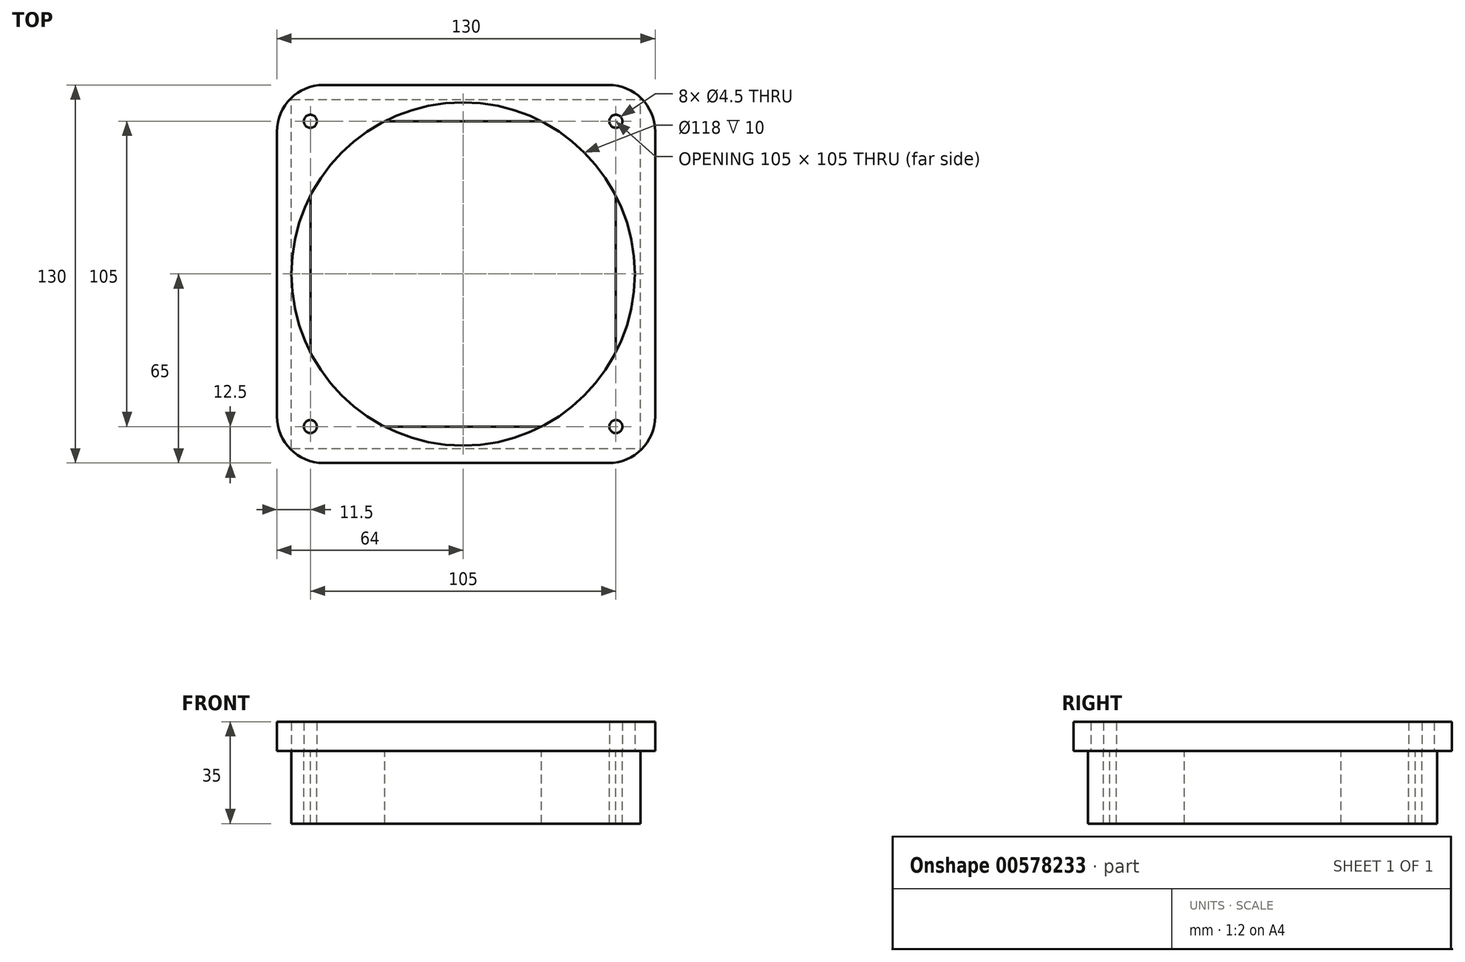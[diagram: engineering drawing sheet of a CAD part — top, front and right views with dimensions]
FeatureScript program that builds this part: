
annotation { "Feature Type Name" : "Feature", "Feature Type Description" : "" }
export const myFeature = defineFeature(function(context is Context, id is Id, definition is map)
    precondition{}
    {
        {
            var Q0;
            Q0=qCreatedBy(makeId("Top.planeOp"),FACE);
            var sketch = newSketch(context, id + "F0", { "sketchPlane" : qUnion([Q0])});
            skLineSegment(sketch, "E0.bottom", {"start": v(-59, -60) * mm, "end": v(61, -60) * mm});
            skLineSegment(sketch, "E0.top", {"start": v(-59, 60) * mm, "end": v(61, 60) * mm});
            skLineSegment(sketch, "E0.left", {"start": v(-59, -60) * mm, "end": v(-59, 60) * mm});
            skLineSegment(sketch, "E0.right", {"start": v(61, -60) * mm, "end": v(61, 60) * mm});
            skLineSegment(sketch, "E1.bottom", {"start": v(-52.5, -52.5) * mm, "end": v(52.5, -52.5) * mm});
            skLineSegment(sketch, "E1.top", {"start": v(-52.5, 52.5) * mm, "end": v(52.5, 52.5) * mm});
            skLineSegment(sketch, "E1.left", {"start": v(-52.5, -52.5) * mm, "end": v(-52.5, 52.5) * mm});
            skLineSegment(sketch, "E1.right", {"start": v(52.5, -52.5) * mm, "end": v(52.5, 52.5) * mm});
            skCircle(sketch, "E2", {"center": v(-52.5, 52.5) * mm, "radius": 2.25 * mm});
            skCircle(sketch, "E3", {"center": v(52.5, 52.5) * mm, "radius": 2.25 * mm});
            skCircle(sketch, "E4", {"center": v(-52.5, -52.5) * mm, "radius": 2.25 * mm});
            skCircle(sketch, "E5", {"center": v(52.5, -52.5) * mm, "radius": 2.25 * mm});
            skCircle(sketch, "E6", {"center": v(0, 0) * mm, "radius": 59 * mm});
            skLineSegment(sketch, "E7.0", {"start": v(-64, -65) * mm, "end": v(-64, 65) * mm});
            skLineSegment(sketch, "E7.1", {"start": v(-64, -65) * mm, "end": v(66, -65) * mm});
            skLineSegment(sketch, "E7.2", {"start": v(66, -65) * mm, "end": v(66, 65) * mm});
            skLineSegment(sketch, "E7.3", {"start": v(-64, 65) * mm, "end": v(66, 65) * mm});
            skSolve(sketch);
        }
        {
            var Q0;
            {var subQ0=sQuery(id+"F0.wireOp",EDGE,"E2");var subQ1=sQuery(id+"F0.wireOp",EDGE,"E1.top");var subQ2=makeQuery(id+"F0.imprint","INTERSECT",VERTEX,{"derivedFrom":[subQ1,subQ0]});Q0=makeQuery(id+"F0.imprint","IMPRINT",FACE,{"disambiguationData":[TD([[makeQuery(id+"F0.imprint","IMPRINT",EDGE,{"disambiguationData":[TD([[subQ2,-1.0]])],"derivedFrom":subQ1}),-1.0]])]});}
            var Q1;
            {var subQ16=sQuery(id+"F0.wireOp",EDGE,"E0.bottom");Q1=makeQuery(id+"F0.imprint","IMPRINT",FACE,{"disambiguationData":[TD([[makeQuery(id+"F0.imprint","IMPRINT",EDGE,{"derivedFrom":subQ16}),1.0]])]});}
            var Q2;
            {var subQ0=sQuery(id+"F0.wireOp",EDGE,"E4");var subQ1=sQuery(id+"F0.wireOp",EDGE,"E1.bottom");var subQ2=makeQuery(id+"F0.imprint","INTERSECT",VERTEX,{"derivedFrom":[subQ1,subQ0]});Q2=makeQuery(id+"F0.imprint","IMPRINT",FACE,{"disambiguationData":[TD([[makeQuery(id+"F0.imprint","IMPRINT",EDGE,{"disambiguationData":[TD([[subQ2,-1.0]])],"derivedFrom":subQ1}),1.0]])]});}
            var Q3;
            {var subQ0=sQuery(id+"F0.wireOp",EDGE,"E6");var subQ1=sQuery(id+"F0.wireOp",EDGE,"E1.bottom");var subQ2=makeQuery(id+"F0.imprint","INTERSECT",VERTEX,{"disambiguationData":[OD(0.0)],"derivedFrom":[subQ1,subQ0]});Q3=makeQuery(id+"F0.imprint","IMPRINT",FACE,{"disambiguationData":[TD([[makeQuery(id+"F0.imprint","IMPRINT",EDGE,{"disambiguationData":[TD([[subQ2,-1.0]])],"derivedFrom":subQ1}),-1.0]])]});}
            var Q4;
            {var subQ0=sQuery(id+"F0.wireOp",EDGE,"E6");var subQ1=sQuery(id+"F0.wireOp",EDGE,"E1.top");var subQ2=makeQuery(id+"F0.imprint","INTERSECT",VERTEX,{"disambiguationData":[OD(0.0)],"derivedFrom":[subQ1,subQ0]});Q4=makeQuery(id+"F0.imprint","IMPRINT",FACE,{"disambiguationData":[TD([[makeQuery(id+"F0.imprint","IMPRINT",EDGE,{"disambiguationData":[TD([[subQ2,-1.0]])],"derivedFrom":subQ1}),1.0]])]});}
            var Q5;
            {var subQ0=sQuery(id+"F0.wireOp",EDGE,"E6");var subQ1=sQuery(id+"F0.wireOp",EDGE,"E1.top");var subQ2=makeQuery(id+"F0.imprint","INTERSECT",VERTEX,{"disambiguationData":[OD(1.0)],"derivedFrom":[subQ1,subQ0]});Q5=makeQuery(id+"F0.imprint","IMPRINT",FACE,{"disambiguationData":[TD([[makeQuery(id+"F0.imprint","IMPRINT",EDGE,{"disambiguationData":[TD([[subQ2,-1.0]])],"derivedFrom":subQ1}),-1.0]])]});}
            var Q6;
            {var subQ0=sQuery(id+"F0.wireOp",EDGE,"E6");var subQ1=sQuery(id+"F0.wireOp",EDGE,"E1.right");var subQ2=makeQuery(id+"F0.imprint","INTERSECT",VERTEX,{"disambiguationData":[OD(0.0)],"derivedFrom":[subQ1,subQ0]});Q6=makeQuery(id+"F0.imprint","IMPRINT",FACE,{"disambiguationData":[TD([[makeQuery(id+"F0.imprint","IMPRINT",EDGE,{"disambiguationData":[TD([[subQ2,-1.0]])],"derivedFrom":subQ1}),-1.0]])]});}
            var Q7;
            {var subQ0=sQuery(id+"F0.wireOp",EDGE,"E6");var subQ1=sQuery(id+"F0.wireOp",EDGE,"E1.bottom");var subQ2=makeQuery(id+"F0.imprint","INTERSECT",VERTEX,{"disambiguationData":[OD(1.0)],"derivedFrom":[subQ1,subQ0]});Q7=makeQuery(id+"F0.imprint","IMPRINT",FACE,{"disambiguationData":[TD([[makeQuery(id+"F0.imprint","IMPRINT",EDGE,{"disambiguationData":[TD([[subQ2,-1.0]])],"derivedFrom":subQ1}),1.0]])]});}
            var Q8;
            {var subQ0=sQuery(id+"F0.wireOp",EDGE,"E6");var subQ1=sQuery(id+"F0.wireOp",EDGE,"E1.left");var subQ2=makeQuery(id+"F0.imprint","INTERSECT",VERTEX,{"disambiguationData":[OD(0.0)],"derivedFrom":[subQ1,subQ0]});Q8=makeQuery(id+"F0.imprint","IMPRINT",FACE,{"disambiguationData":[TD([[makeQuery(id+"F0.imprint","IMPRINT",EDGE,{"disambiguationData":[TD([[subQ2,-1.0]])],"derivedFrom":subQ1}),1.0]])]});}
            extrude(context, id + "F1", {"entities" : qUnion([Q0, Q1, Q2, Q3, Q4, Q5, Q6, Q7, Q8]), "oppositeDirection" : true, "depth" : 25 * mm, "offsetDistance" : 25 * mm});
        }
        {
            var Q0;
            {var subQ3=sQuery(id+"F0.wireOp",EDGE,"E0.bottom");Q0=makeQuery(id+"F0.imprint","IMPRINT",FACE,{"disambiguationData":[TD([[makeQuery(id+"F0.imprint","IMPRINT",EDGE,{"derivedFrom":subQ3}),-1.0]])]});}
            var Q1;
            {var subQ0=sQuery(id+"F0.wireOp",EDGE,"E2");var subQ1=sQuery(id+"F0.wireOp",EDGE,"E1.top");var subQ2=makeQuery(id+"F0.imprint","INTERSECT",VERTEX,{"derivedFrom":[subQ1,subQ0]});Q1=makeQuery(id+"F0.imprint","IMPRINT",FACE,{"disambiguationData":[TD([[makeQuery(id+"F0.imprint","IMPRINT",EDGE,{"disambiguationData":[TD([[subQ2,-1.0]])],"derivedFrom":subQ1}),-1.0]])]});}
            var Q2;
            {var subQ16=sQuery(id+"F0.wireOp",EDGE,"E0.bottom");Q2=makeQuery(id+"F0.imprint","IMPRINT",FACE,{"disambiguationData":[TD([[makeQuery(id+"F0.imprint","IMPRINT",EDGE,{"derivedFrom":subQ16}),1.0]])]});}
            var Q3;
            {var subQ0=sQuery(id+"F0.wireOp",EDGE,"E6");var subQ1=sQuery(id+"F0.wireOp",EDGE,"E1.top");var subQ2=makeQuery(id+"F0.imprint","INTERSECT",VERTEX,{"disambiguationData":[OD(1.0)],"derivedFrom":[subQ1,subQ0]});Q3=makeQuery(id+"F0.imprint","IMPRINT",FACE,{"disambiguationData":[TD([[makeQuery(id+"F0.imprint","IMPRINT",EDGE,{"disambiguationData":[TD([[subQ2,-1.0]])],"derivedFrom":subQ1}),-1.0]])]});}
            var Q4;
            {var subQ0=sQuery(id+"F0.wireOp",EDGE,"E6");var subQ1=sQuery(id+"F0.wireOp",EDGE,"E1.bottom");var subQ2=makeQuery(id+"F0.imprint","INTERSECT",VERTEX,{"disambiguationData":[OD(1.0)],"derivedFrom":[subQ1,subQ0]});Q4=makeQuery(id+"F0.imprint","IMPRINT",FACE,{"disambiguationData":[TD([[makeQuery(id+"F0.imprint","IMPRINT",EDGE,{"disambiguationData":[TD([[subQ2,-1.0]])],"derivedFrom":subQ1}),1.0]])]});}
            var Q5;
            {var subQ0=sQuery(id+"F0.wireOp",EDGE,"E4");var subQ1=sQuery(id+"F0.wireOp",EDGE,"E1.bottom");var subQ2=makeQuery(id+"F0.imprint","INTERSECT",VERTEX,{"derivedFrom":[subQ1,subQ0]});Q5=makeQuery(id+"F0.imprint","IMPRINT",FACE,{"disambiguationData":[TD([[makeQuery(id+"F0.imprint","IMPRINT",EDGE,{"disambiguationData":[TD([[subQ2,-1.0]])],"derivedFrom":subQ1}),1.0]])]});}
            extrude(context, id + "F2", {"entities" : qUnion([Q0, Q1, Q2, Q3, Q4, Q5]), "depth" : 10 * mm, "offsetDistance" : 25 * mm});
        }
        {
            var Q0;
            Q0=makeQuery(id+"F2.opExtrude","SWEPT_EDGE",EDGE,{"disambiguationData":[OSD([sQuery(id+"F0.wireOp",EDGE,"E7.0"),sQuery(id+"F0.wireOp",EDGE,"E7.3")])]});
            var Q1;
            Q1=makeQuery(id+"F2.opExtrude","SWEPT_EDGE",EDGE,{"disambiguationData":[OSD([sQuery(id+"F0.wireOp",EDGE,"E7.0"),sQuery(id+"F0.wireOp",EDGE,"E7.1")])]});
            var Q2;
            Q2=makeQuery(id+"F2.opExtrude","SWEPT_EDGE",EDGE,{"disambiguationData":[OSD([sQuery(id+"F0.wireOp",EDGE,"E7.1"),sQuery(id+"F0.wireOp",EDGE,"E7.2")])]});
            var Q3;
            Q3=makeQuery(id+"F2.opExtrude","SWEPT_EDGE",EDGE,{"disambiguationData":[OSD([sQuery(id+"F0.wireOp",EDGE,"E7.2"),sQuery(id+"F0.wireOp",EDGE,"E7.3")])]});
            fillet(context, id + "F3", {"entities" : qUnion([Q0, Q1, Q2, Q3]), "radius" : 16 * mm, "tangentPropagation" : true, "allowEdgeOverflow" : false});
        }
    });
